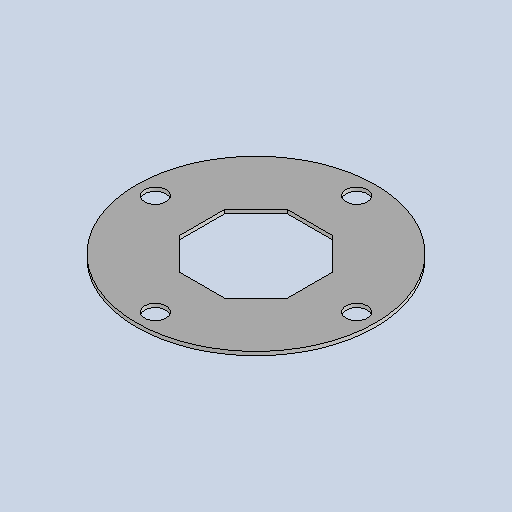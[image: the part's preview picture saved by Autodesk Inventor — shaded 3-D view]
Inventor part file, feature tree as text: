
AUTODESK INVENTOR PART (.ipt)
format: ipt  version: 2025.1 (Build 291241020, 241B)  size: 171,520 bytes
history: native  units: mm
features: other x4, sketch x2, sheet_metal_op x1, pattern_circular x1
ambient origin geometry x8: Origin, YZ Plane, XZ Plane, XY Plane, X Axis, Y Axis, Z Axis, Center Point
bodies: Body1 (feature_tree)
feature tree (8):
  sheet_metal_op  "Face3"
  pattern_circular  "Circular Pattern1"  Count=50  [1 undecoded]
  other  "Corner Chamfer2"
  sketch  "Sketch1"  dims[d156=3.0mm]
  other  "Plate5"
  sketch  "Sketch7"  dims[d157=190.0mm d158=86.0mm d159=86.0mm d160=17.0mm d161=80.0mm d162=3.0mm d163=0.0mm d164=40.0mm d165=360.0deg d167=25.0mm d168=6.0mm d169=45.0deg]
  other  "Cut1"
  other  "Definition1"
note: 1 required parameter value undecoded (feature->parameter linkage not recoverable at this tier; creation-order binding heuristic only, values carry confidence <= 0.55)
